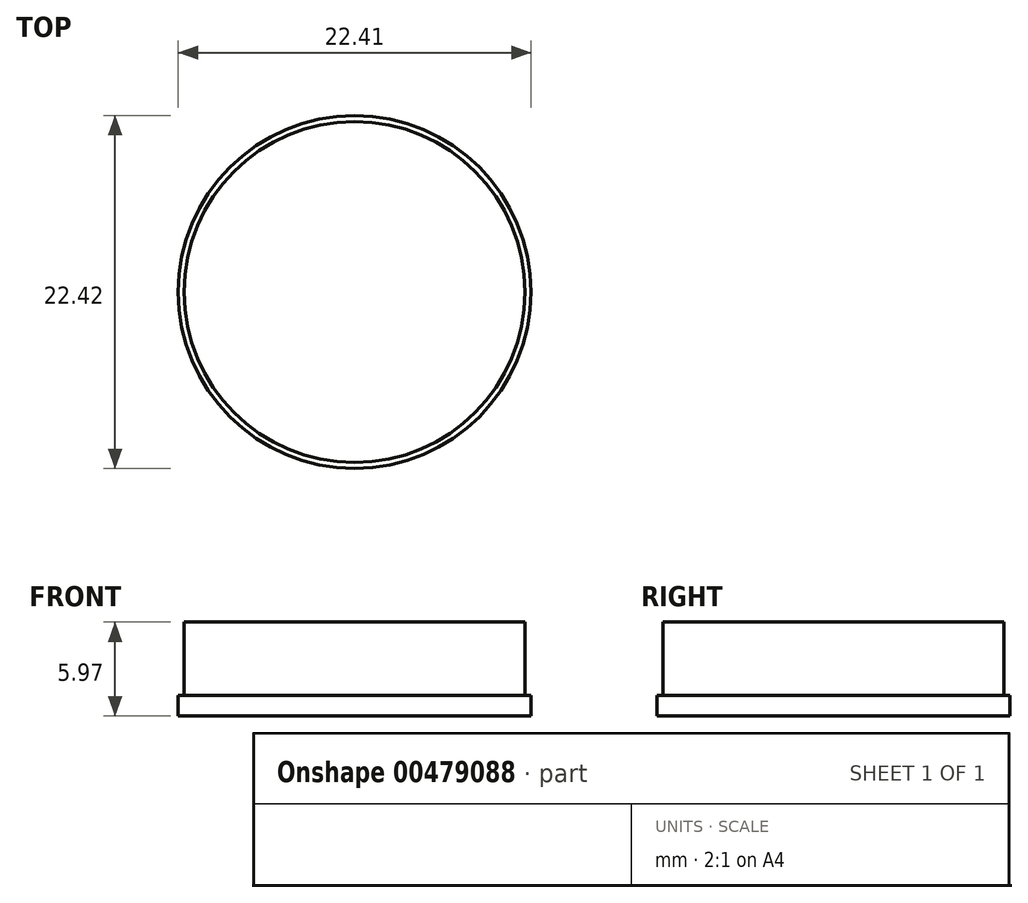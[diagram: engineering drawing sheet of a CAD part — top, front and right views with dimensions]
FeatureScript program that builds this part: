
annotation { "Feature Type Name" : "Feature", "Feature Type Description" : "" }
export const myFeature = defineFeature(function(context is Context, id is Id, definition is map)
    precondition{}
    {
        {
            var Q0;
            Q0=qCreatedBy(makeId("Front.planeOp"),FACE);
            var sketch = newSketch(context, id + "F0", { "sketchPlane" : qUnion([Q0])});
            skLineSegment(sketch, "E0", {"start": v(10.08, -6.08) * mm, "end": v(-4.92, -6.08) * mm});
            skLineSegment(sketch, "E1", {"start": v(-4.92, -6.08) * mm, "end": v(-4.92, 3.92) * mm});
            skLineSegment(sketch, "E2", {"start": v(-4.92, 3.92) * mm, "end": v(-0.92, 3.92) * mm});
            skLineSegment(sketch, "E3", {"start": v(-0.92, 3.92) * mm, "end": v(-0.92, 0.34) * mm});
            skLineSegment(sketch, "E4", {"start": v(-0.92, 0.34) * mm, "end": v(-1.22, 0.34) * mm});
            skLineSegment(sketch, "E5", {"start": v(-1.22, 0.34) * mm, "end": v(-1.22, -1.17) * mm});
            skLineSegment(sketch, "E6", {"start": v(-1.22, -1.17) * mm, "end": v(10.08, -1.17) * mm});
            skLineSegment(sketch, "E7", {"start": v(10.08, -1.17) * mm, "end": v(10.08, -6.08) * mm});
            skSolve(sketch);
        }
        {
            var Q0;
            Q0=makeQuery(id+"F0.imprint","IMPRINT",FACE,{"disambiguationData":[TD([[makeQuery(id+"F0.imprint","IMPRINT",EDGE,{"derivedFrom":sQuery(id+"F0.wireOp",EDGE,"E0")}),-1.0]])]});
            var sketch = newSketch(context, id + "F1", { "sketchPlane" : qUnion([Q0])});
            skLineSegment(sketch, "E8", {"start": v(-0.77, 4.87) * mm, "end": v(-0.77, 0.22) * mm});
            skLineSegment(sketch, "E9", {"start": v(-0.77, 0.22) * mm, "end": v(-1.15, 0.22) * mm});
            skLineSegment(sketch, "E10", {"start": v(-1.15, 0.22) * mm, "end": v(-1.15, -1.1) * mm});
            skLineSegment(sketch, "E11", {"start": v(-1.15, -1.1) * mm, "end": v(10.05, -1.1) * mm});
            skLineSegment(sketch, "E12", {"start": v(10.05, -1.1) * mm, "end": v(10.05, 4.87) * mm});
            skLineSegment(sketch, "E13", {"start": v(10.05, 4.87) * mm, "end": v(-0.77, 4.87) * mm});
            skSolve(sketch);
        }
        {
            var Q0;
            Q0=makeQuery(id+"F1.imprint","IMPRINT",FACE,{"disambiguationData":[TD([[makeQuery(id+"F1.imprint","IMPRINT",EDGE,{"derivedFrom":sQuery(id+"F1.wireOp",EDGE,"E8")}),1.0]])]});
            var Q1;
            Q1=sQuery(id+"F1.wireOp",EDGE,"E12");
            revolve(context, id + "F2", {"entities" : qUnion([Q0]), "axis" : qUnion([Q1]), "revolveType" : RevolveType.FULL});
        }
    });
